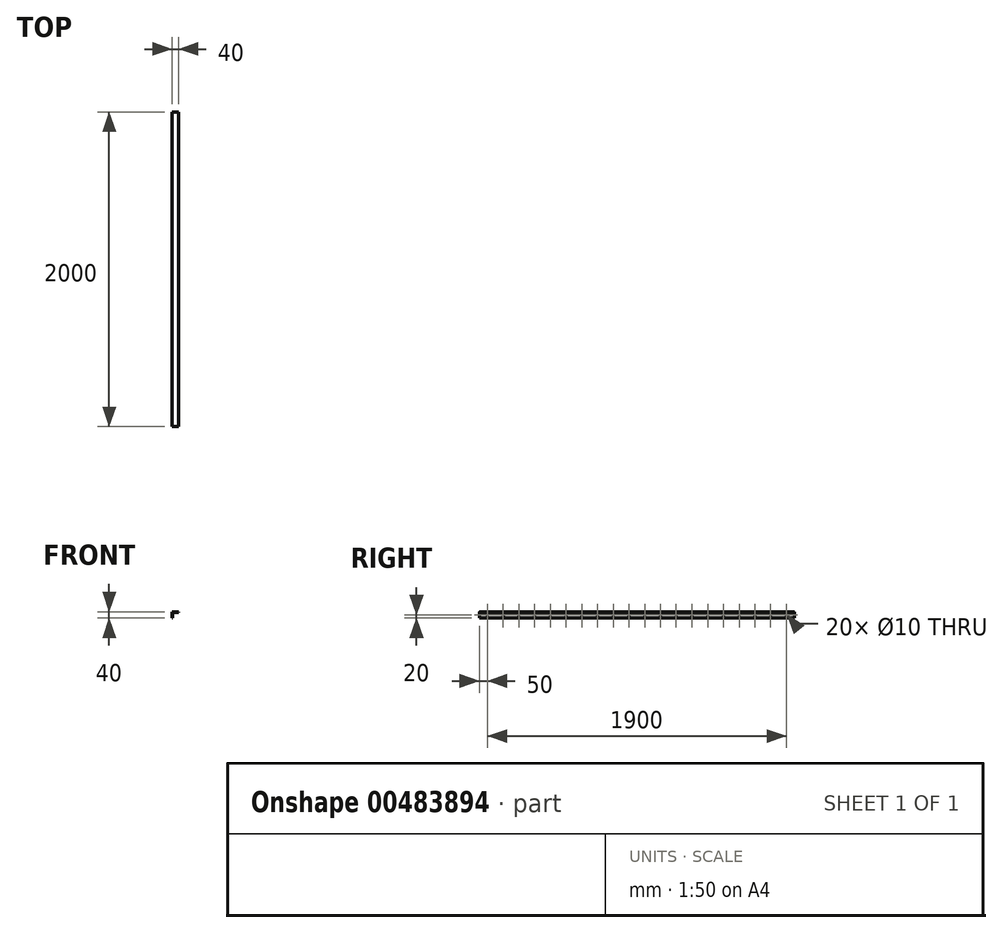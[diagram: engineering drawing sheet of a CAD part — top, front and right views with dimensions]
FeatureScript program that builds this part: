
annotation { "Feature Type Name" : "Feature", "Feature Type Description" : "" }
export const myFeature = defineFeature(function(context is Context, id is Id, definition is map)
    precondition{}
    {
        {
            var Q0;
            Q0=qCreatedBy(makeId("Front.planeOp"),FACE);
            var sketch = newSketch(context, id + "F0", { "sketchPlane" : qUnion([Q0])});
            skLineSegment(sketch, "E0", {"start": v(0, 0) * mm, "end": v(40, 0) * mm});
            skLineSegment(sketch, "E1", {"start": v(0, 0) * mm, "end": v(0, -40) * mm});
            skLineSegment(sketch, "E2", {"start": v(0, -40) * mm, "end": v(3, -40) * mm});
            skLineSegment(sketch, "E3", {"start": v(40, 0) * mm, "end": v(40, -3) * mm});
            skLineSegment(sketch, "E4", {"start": v(40, -3) * mm, "end": v(8, -3) * mm});
            skLineSegment(sketch, "E5", {"start": v(3, -8) * mm, "end": v(3, -40) * mm});
            skPoint(sketch, "E6.visualSharp", {"position": v(3, -3) * mm});
            skArc(sketch, "E6.filletArc", {"start": v(8, -3) * mm, "mid": v(4.46, -4.46) * mm, "end": v(3, -8) * mm});
            skSolve(sketch);
        }
        {
            var Q0;
            Q0=makeQuery(id+"F0.imprint","IMPRINT",FACE,{"disambiguationData":[TD([[makeQuery(id+"F0.imprint","IMPRINT",EDGE,{"derivedFrom":sQuery(id+"F0.wireOp",EDGE,"E0")}),-1.0]])]});
            extrude(context, id + "F1", {"entities" : qUnion([Q0]), "depth" : 2000 * mm});
        }
        {
            var Q0;
            Q0=makeQuery(id+"F1.opExtrude","SWEPT_FACE",FACE,{"disambiguationData":[OSD([sQuery(id+"F0.wireOp",EDGE,"E1")])]});
            var sketch = newSketch(context, id + "F2", { "sketchPlane" : qUnion([Q0])});
            skCircle(sketch, "E7", {"center": v(50, -20) * mm, "radius": 5 * mm});
            skPoint(sketch, "E7.centerSnap0", {"position": v(0, -20) * mm});
            skCircle(sketch, "E8.1.0.0", {"center": v(150, -20) * mm, "radius": 5 * mm});
            skCircle(sketch, "E8.2.0.0", {"center": v(250, -20) * mm, "radius": 5 * mm});
            skCircle(sketch, "E8.3.0.0", {"center": v(350, -20) * mm, "radius": 5 * mm});
            skCircle(sketch, "E8.4.0.0", {"center": v(450, -20) * mm, "radius": 5 * mm});
            skCircle(sketch, "E8.5.0.0", {"center": v(550, -20) * mm, "radius": 5 * mm});
            skCircle(sketch, "E8.6.0.0", {"center": v(650, -20) * mm, "radius": 5 * mm});
            skCircle(sketch, "E8.7.0.0", {"center": v(750, -20) * mm, "radius": 5 * mm});
            skCircle(sketch, "E8.8.0.0", {"center": v(850, -20) * mm, "radius": 5 * mm});
            skCircle(sketch, "E8.9.0.0", {"center": v(950, -20) * mm, "radius": 5 * mm});
            skCircle(sketch, "E8.10.0.0", {"center": v(1050, -20) * mm, "radius": 5 * mm});
            skCircle(sketch, "E8.11.0.0", {"center": v(1150, -20) * mm, "radius": 5 * mm});
            skCircle(sketch, "E8.12.0.0", {"center": v(1250, -20) * mm, "radius": 5 * mm});
            skCircle(sketch, "E8.13.0.0", {"center": v(1350, -20) * mm, "radius": 5 * mm});
            skCircle(sketch, "E8.14.0.0", {"center": v(1450, -20) * mm, "radius": 5 * mm});
            skCircle(sketch, "E8.15.0.0", {"center": v(1550, -20) * mm, "radius": 5 * mm});
            skCircle(sketch, "E8.16.0.0", {"center": v(1650, -20) * mm, "radius": 5 * mm});
            skCircle(sketch, "E8.17.0.0", {"center": v(1750, -20) * mm, "radius": 5 * mm});
            skCircle(sketch, "E8.18.0.0", {"center": v(1850, -20) * mm, "radius": 5 * mm});
            skCircle(sketch, "E8.19.0.0", {"center": v(1950, -20) * mm, "radius": 5 * mm});
            skCircle(sketch, "E8.20.0.0", {"center": v(2050, -20) * mm, "radius": 5 * mm});
            skCircle(sketch, "E8.21.0.0", {"center": v(2150, -20) * mm, "radius": 5 * mm});
            skCircle(sketch, "E8.22.0.0", {"center": v(2250, -20) * mm, "radius": 5 * mm});
            skCircle(sketch, "E8.23.0.0", {"center": v(2350, -20) * mm, "radius": 5 * mm});
            skCircle(sketch, "E8.24.0.0", {"center": v(2450, -20) * mm, "radius": 5 * mm});
            skLineSegment(sketch, "E8.direction1", {"start": v(50, -20) * mm, "end": v(150, -20) * mm, "construction": true});
            skSolve(sketch);
        }
        {
            var Q0;
            Q0 = qSketchRegion(id + "F2", true);
            var Q1;
            Q1=makeQuery(id+"F1.opExtrude","SWEPT_FACE",FACE,{"disambiguationData":[OSD([sQuery(id+"F0.wireOp",EDGE,"E5")])]});
            extrude(context, id + "F3", {"entities" : qUnion([Q0]), "operationType" : NewBodyOperationType.REMOVE, "endBound" : BoundingType.UP_TO_SURFACE, "oppositeDirection" : true, "endBoundEntityFace" : qUnion([Q1]), "depth" : 25 * mm});
        }
    });
